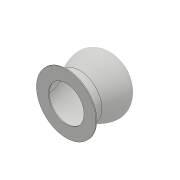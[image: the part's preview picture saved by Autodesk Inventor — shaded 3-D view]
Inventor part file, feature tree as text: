
AUTODESK INVENTOR PART (.ipt)
format: ipt  version: 2018 (Build 220112000, 112)  size: 316,928 bytes
history: native  units: mm
features: sketch x4, extrude x2, revolve x1, shell x1, hole x1, fillet x1, projected_geometry x1
ambient origin geometry x8: Origin, YZ Plane, XZ Plane, XY Plane, X Axis, Y Axis, Z Axis, Center Point
bodies: Solid1 (feature_tree)
feature tree (11):
  revolve  "Revolution1"  [1 undecoded]
  sketch  "Sketch2"  dims[d3=21.0mm d4=28.0mm]
  shell  "Shell1"  Thickness=38.0mm
  extrude  "Extrusion3"  Depth=28.0mm
  hole  "Hole2"  [1 undecoded]
  extrude  "Extrusion2"  Depth=12.5mm
  fillet  "Fillet2"  Radius=21.0mm
  sketch  "Sketch1"  dims[d0=55.0mm d1=33.0mm d2=38.0mm]
  sketch  "Sketch5"  dims[d5=20.0mm d6=22.0mm]
  sketch  "Sketch6"  dims[d7=90.0deg d8=12.5mm d9=21.0mm d10=6.5mm d11=1.0mm d26=1.567mm d27=4.0mm d28=6.3mm d29=2.0mm d30=90.0deg d31=6.3mm d32=20.594885mm d33=12.0mm d34=1.0mm d35=0.0mm d36=70.0mm d37=1.0mm d38=0.0mm d48=11.0mm]
  projected_geometry  "Project Cut Edges2"
note: 2 required parameter values undecoded (feature->parameter linkage not recoverable at this tier; creation-order binding heuristic only, values carry confidence <= 0.55)